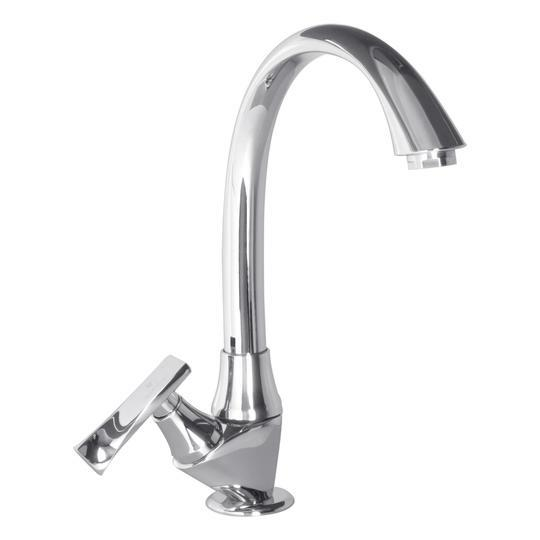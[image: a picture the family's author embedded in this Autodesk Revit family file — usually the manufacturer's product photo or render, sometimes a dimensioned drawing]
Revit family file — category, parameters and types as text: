
# Revit family: 01-2837-11 LLAVE MOVIL MESA METAL COLECCION PRISTINA
name_source: partatom
category: Plumbing Fixtures
revit_build: Autodesk Revit 2018 (Build: 20170223_1515(x64)
units: mm (PartAtom-declared; Revit-internal decimal feet)

## family parameters
Cut with Voids When Loaded = No
Host = Face
OmniClass Number = 23.31.11.00
Part Type = Normal
Room Calculation Point = No
Round Connector Dimension = Use Diameter
Shared = No

## types (1)
- 01-2837-11
    Alto Aireador = 244 mm  [stored 0.800525 ft]
    Alto brazo = 302 mm  [stored 0.990814 ft]
    Ancho a manija = 75 mm
    Ancho brazo = 137 mm  [stored 0.449475 ft]
    CW Connection = Yes
    Default Elevation = 0 mm  [stored 0 ft]
    Description = Monomando
    HW Connection = Yes
    Link Ficha Tecnica = http://infotecnica.gricol.com
    Manufacturer = Gricol
    Model = 01-2837-11
    Plástico - ABS Cromado = Plastico ABS Cromado
    Product Name = LLAVE MOVIL MESA METAL COLECCION PRISTINA
    Type Image = LLAVE MOVIL MESA METAL COLECCION PRISTINA.jpg
    URL = https://www.gricol.com
    Vent Connection = No
    Waste Connection = No

note: [stored X ft] marks values corroborated as IEEE doubles in the binary element streams (Revit-internal decimal feet)

## geometry (parser evidence)
native form markers: Blend x2, Sweep x6
no freeform markers — native parametric forms only
